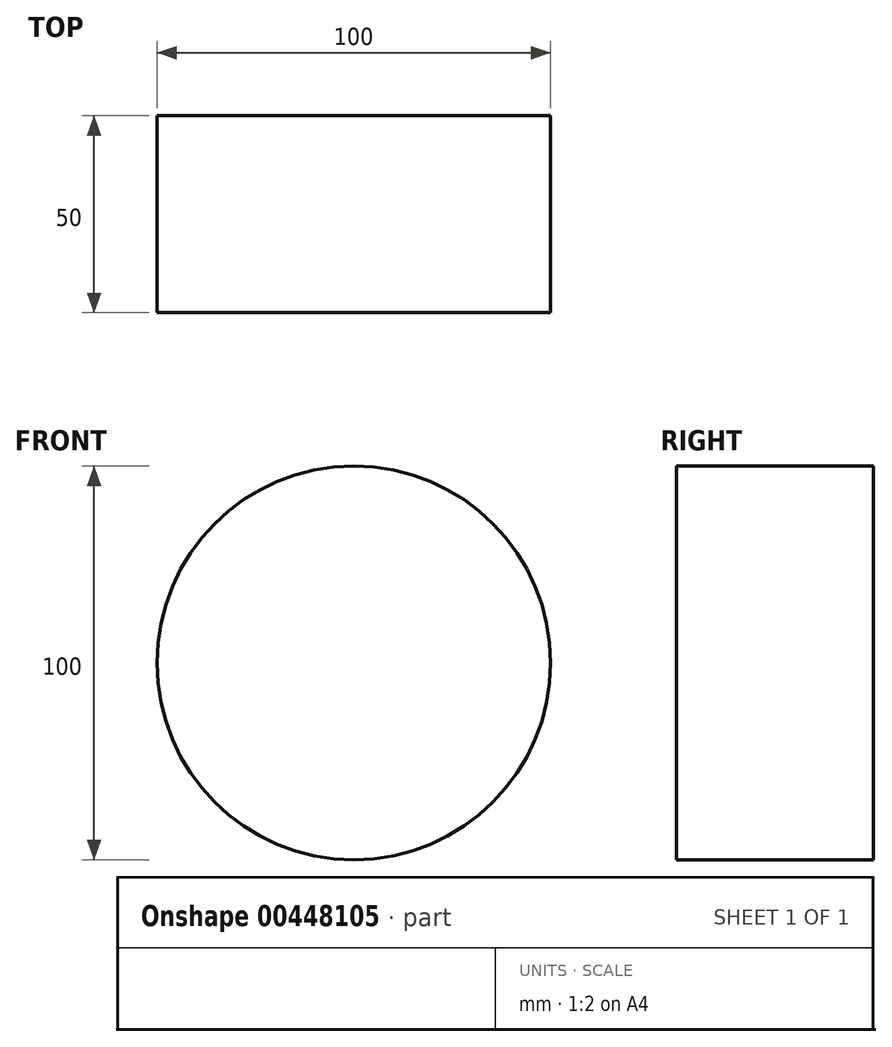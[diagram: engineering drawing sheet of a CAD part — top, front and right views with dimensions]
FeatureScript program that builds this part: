
annotation { "Feature Type Name" : "Feature", "Feature Type Description" : "" }
export const myFeature = defineFeature(function(context is Context, id is Id, definition is map)
    precondition{}
    {
        {
            var Q0;
            Q0=qCreatedBy(makeId("Front.planeOp"),FACE);
            var sketch = newSketch(context, id + "F0", { "sketchPlane" : qUnion([Q0])});
            skCircle(sketch, "E0", {"center": v(0, 0) * mm, "radius": 50 * mm});
            skSolve(sketch);
        }
        {
            var Q0;
            Q0=makeQuery(id+"F0.imprint","IMPRINT",FACE,{"disambiguationData":[TD([[makeQuery(id+"F0.imprint","IMPRINT",EDGE,{"derivedFrom":sQuery(id+"F0.wireOp",EDGE,"E0")}),1.0]])]});
            extrude(context, id + "F1", {"entities" : qUnion([Q0]), "endBound" : BoundingType.SYMMETRIC, "depth" : 50 * mm});
        }
    });
